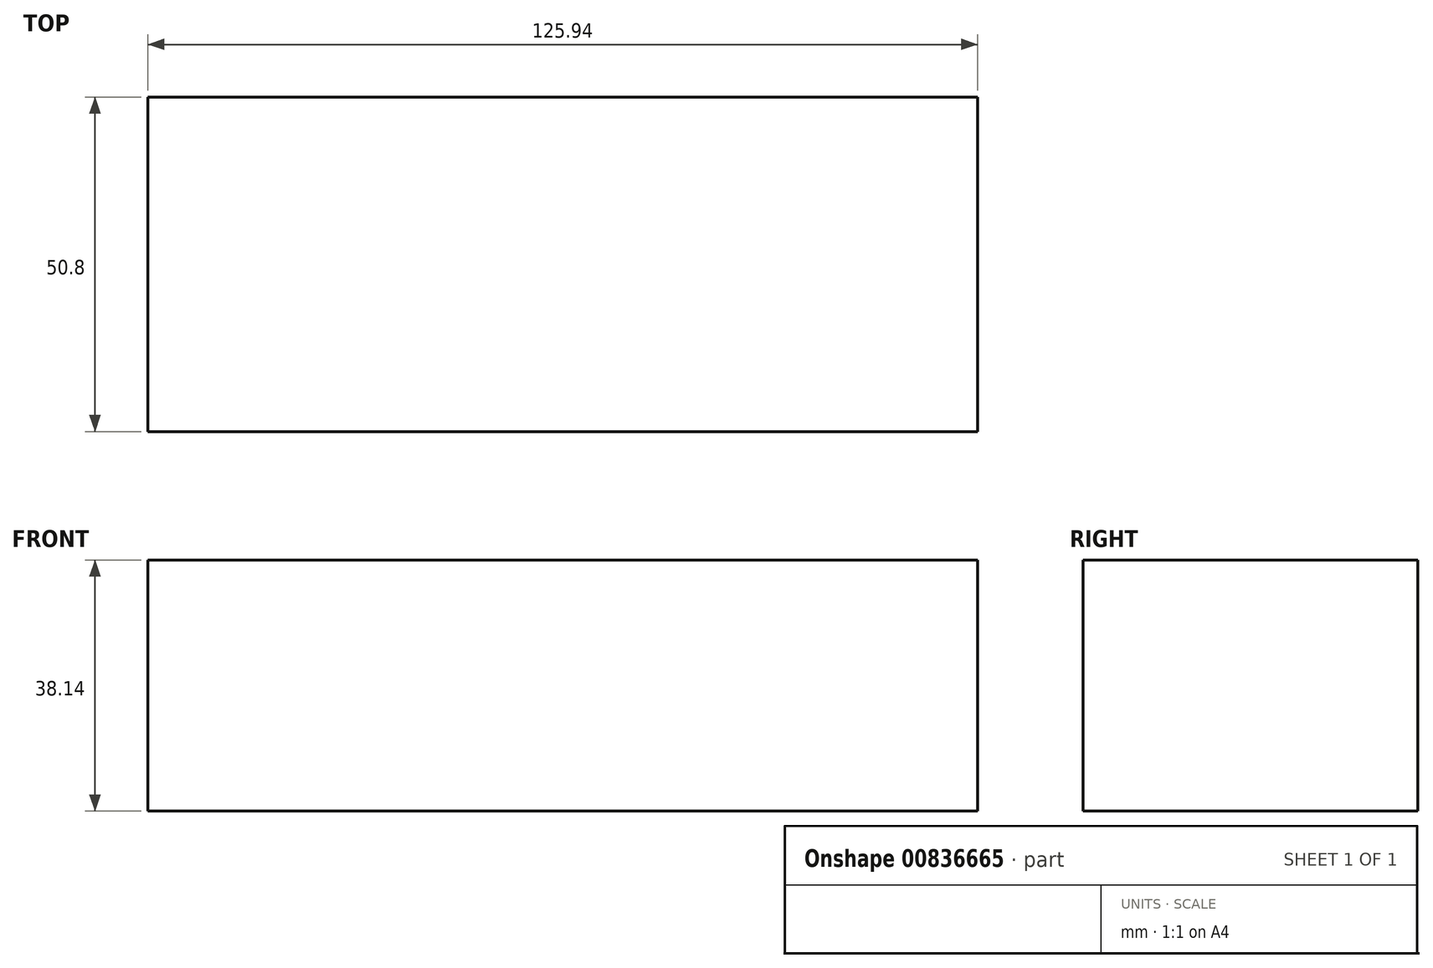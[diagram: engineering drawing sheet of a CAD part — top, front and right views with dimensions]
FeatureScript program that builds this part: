
annotation { "Feature Type Name" : "Feature", "Feature Type Description" : "" }
export const myFeature = defineFeature(function(context is Context, id is Id, definition is map)
    precondition{}
    {
        {
            var Q0;
            Q0=qCreatedBy(makeId("Front.planeOp"),FACE);
            var sketch = newSketch(context, id + "F0", { "sketchPlane" : qUnion([Q0])});
            skLineSegment(sketch, "E0.bottom", {"start": v(62.97, 19.07) * mm, "end": v(-62.97, 19.07) * mm});
            skLineSegment(sketch, "E0.top", {"start": v(62.97, -19.07) * mm, "end": v(-62.97, -19.07) * mm});
            skLineSegment(sketch, "E0.left", {"start": v(62.97, 19.07) * mm, "end": v(62.97, -19.07) * mm});
            skLineSegment(sketch, "E0.right", {"start": v(-62.97, 19.07) * mm, "end": v(-62.97, -19.07) * mm});
            skPoint(sketch, "E0.middle", {"position": v(0, 0) * mm});
            skSolve(sketch);
        }
        {
            var Q0;
            Q0 = qSketchRegion(id + "F0", true);
            extrude(context, id + "F1", {"entities" : qUnion([Q0]), "endBound" : BoundingType.SYMMETRIC, "depth" : 50.8 * mm, "offsetDistance" : 25.4 * mm});
        }
    });
